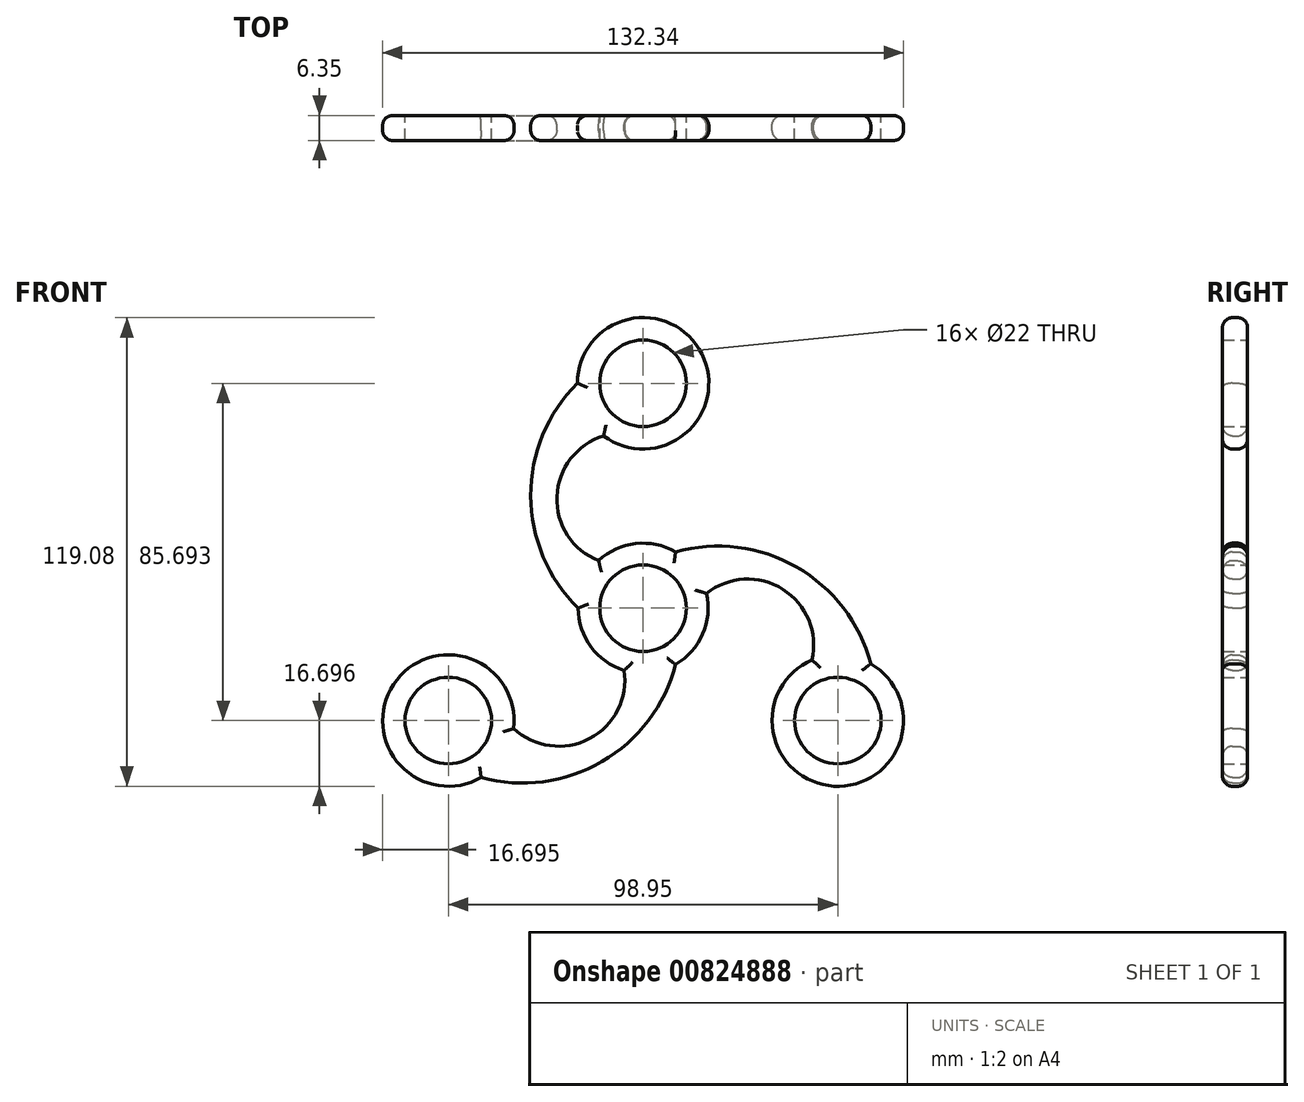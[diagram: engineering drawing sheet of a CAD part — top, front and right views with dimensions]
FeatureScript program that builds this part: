
annotation { "Feature Type Name" : "Feature", "Feature Type Description" : "" }
export const myFeature = defineFeature(function(context is Context, id is Id, definition is map)
    precondition{}
    {
        {
            var Q0;
            Q0=qCreatedBy(makeId("Front.planeOp"),FACE);
            var sketch = newSketch(context, id + "F0", { "sketchPlane" : qUnion([Q0])});
            skCircle(sketch, "E0", {"center": v(0, 0) * mm, "radius": 11 * mm});
            skCircle(sketch, "E1", {"center": v(0, 57.13) * mm, "radius": 11 * mm});
            skArc(sketch, "E2", {"start": v(-16.5, 0) * mm, "mid": v(-13.26, -9.82) * mm, "end": v(-4.8, -15.79) * mm});
            skArc(sketch, "E3", {"start": v(-10.01, 43.77) * mm, "mid": v(14.94, 64.59) * mm, "end": v(-16.7, 57.15) * mm});
            skArc(sketch, "E4", {"start": v(-16.7, 57.15) * mm, "mid": v(-28.55, 28.54) * mm, "end": v(-16.5, 0) * mm});
            skArc(sketch, "E5", {"start": v(-10.01, 43.77) * mm, "mid": v(-21.9, 28.36) * mm, "end": v(-11.27, 12.06) * mm});
            skArc(sketch, "E6.1.0", {"start": v(-32.9, -30.56) * mm, "mid": v(-63.4, -19.36) * mm, "end": v(-41.15, -43.03) * mm});
            skCircle(sketch, "E6.1.1", {"center": v(-49.47, -28.56) * mm, "radius": 11 * mm});
            skArc(sketch, "E6.1.2", {"start": v(-41.15, -43.03) * mm, "mid": v(-10.44, -38.99) * mm, "end": v(8.25, -14.3) * mm});
            skArc(sketch, "E6.1.3", {"start": v(-32.9, -30.56) * mm, "mid": v(-13.61, -33.15) * mm, "end": v(-4.8, -15.79) * mm});
            skArc(sketch, "E6.2.0", {"start": v(42.91, -13.21) * mm, "mid": v(48.47, -45.23) * mm, "end": v(57.84, -14.12) * mm});
            skCircle(sketch, "E6.2.1", {"center": v(49.47, -28.56) * mm, "radius": 11 * mm});
            skArc(sketch, "E6.2.2", {"start": v(57.84, -14.12) * mm, "mid": v(38.99, 10.45) * mm, "end": v(8.25, 14.3) * mm});
            skArc(sketch, "E6.2.3", {"start": v(42.91, -13.21) * mm, "mid": v(35.51, 4.78) * mm, "end": v(16.08, 3.73) * mm});
            skArc(sketch, "E7.trimOffspring", {"start": v(8.25, 14.3) * mm, "mid": v(-1.88, 16.4) * mm, "end": v(-11.27, 12.06) * mm});
            skArc(sketch, "E8.trimOffspring", {"start": v(8.25, -14.3) * mm, "mid": v(15.14, -6.57) * mm, "end": v(16.08, 3.73) * mm});
            skSolve(sketch);
        }
        {
            var Q0;
            Q0=makeQuery(id+"F0.imprint","IMPRINT",FACE,{"disambiguationData":[TD([[makeQuery(id+"F0.imprint","IMPRINT",EDGE,{"derivedFrom":sQuery(id+"F0.wireOp",EDGE,"E0")}),-1.0]])]});
            extrude(context, id + "F1", {"entities" : qUnion([Q0]), "depth" : 6.35 * mm, "offsetDistance" : 25.4 * mm});
        }
        {
            var Q0;
            Q0=makeQuery(id+"F1.opExtrude","CAP_EDGE",EDGE,{"disambiguationData":[OSD([sQuery(id+"F0.wireOp",EDGE,"E6.2.2")])],"isStart":false});
            var Q1;
            Q1=makeQuery(id+"F1.opExtrude","CAP_EDGE",EDGE,{"disambiguationData":[OSD([sQuery(id+"F0.wireOp",EDGE,"E6.2.0")])],"isStart":false});
            var Q2;
            Q2=makeQuery(id+"F1.opExtrude","CAP_EDGE",EDGE,{"disambiguationData":[OSD([sQuery(id+"F0.wireOp",EDGE,"E6.2.3")])],"isStart":false});
            var Q3;
            Q3=makeQuery(id+"F1.opExtrude","CAP_EDGE",EDGE,{"disambiguationData":[OSD([sQuery(id+"F0.wireOp",EDGE,"E7.trimOffspring")])],"isStart":false});
            var Q4;
            Q4=makeQuery(id+"F1.opExtrude","CAP_EDGE",EDGE,{"disambiguationData":[OSD([sQuery(id+"F0.wireOp",EDGE,"E8.trimOffspring")])],"isStart":false});
            var Q5;
            Q5=makeQuery(id+"F1.opExtrude","CAP_EDGE",EDGE,{"disambiguationData":[OSD([sQuery(id+"F0.wireOp",EDGE,"E6.1.2")])],"isStart":false});
            var Q6;
            Q6=makeQuery(id+"F1.opExtrude","CAP_EDGE",EDGE,{"disambiguationData":[OSD([sQuery(id+"F0.wireOp",EDGE,"E6.1.3")])],"isStart":false});
            var Q7;
            Q7=makeQuery(id+"F1.opExtrude","CAP_EDGE",EDGE,{"disambiguationData":[OSD([sQuery(id+"F0.wireOp",EDGE,"E2")])],"isStart":false});
            var Q8;
            Q8=makeQuery(id+"F1.opExtrude","CAP_EDGE",EDGE,{"disambiguationData":[OSD([sQuery(id+"F0.wireOp",EDGE,"E4")])],"isStart":false});
            var Q9;
            Q9=makeQuery(id+"F1.opExtrude","CAP_EDGE",EDGE,{"disambiguationData":[OSD([sQuery(id+"F0.wireOp",EDGE,"E5")])],"isStart":false});
            var Q10;
            Q10=makeQuery(id+"F1.opExtrude","CAP_EDGE",EDGE,{"disambiguationData":[OSD([sQuery(id+"F0.wireOp",EDGE,"E6.1.0")])],"isStart":false});
            var Q11;
            Q11=makeQuery(id+"F1.opExtrude","CAP_EDGE",EDGE,{"disambiguationData":[OSD([sQuery(id+"F0.wireOp",EDGE,"E3")])],"isStart":false});
            fillet(context, id + "F2", {"entities" : qUnion([Q0, Q1, Q2, Q3, Q4, Q5, Q6, Q7, Q8, Q9, Q10, Q11]), "radius" : 2.54 * mm, "tangentPropagation" : true, "allowEdgeOverflow" : false});
        }
        {
            var Q0;
            Q0=makeQuery(id+"F1.opExtrude","CAP_EDGE",EDGE,{"disambiguationData":[OSD([sQuery(id+"F0.wireOp",EDGE,"E3")])],"isStart":true});
            var Q1;
            Q1=makeQuery(id+"F1.opExtrude","CAP_EDGE",EDGE,{"disambiguationData":[OSD([sQuery(id+"F0.wireOp",EDGE,"E4")])],"isStart":true});
            var Q2;
            Q2=makeQuery(id+"F1.opExtrude","CAP_EDGE",EDGE,{"disambiguationData":[OSD([sQuery(id+"F0.wireOp",EDGE,"E5")])],"isStart":true});
            var Q3;
            Q3=makeQuery(id+"F1.opExtrude","CAP_EDGE",EDGE,{"disambiguationData":[OSD([sQuery(id+"F0.wireOp",EDGE,"E7.trimOffspring")])],"isStart":true});
            var Q4;
            Q4=makeQuery(id+"F1.opExtrude","CAP_EDGE",EDGE,{"disambiguationData":[OSD([sQuery(id+"F0.wireOp",EDGE,"E6.2.2")])],"isStart":true});
            var Q5;
            Q5=makeQuery(id+"F1.opExtrude","CAP_EDGE",EDGE,{"disambiguationData":[OSD([sQuery(id+"F0.wireOp",EDGE,"E6.2.3")])],"isStart":true});
            var Q6;
            Q6=makeQuery(id+"F1.opExtrude","CAP_EDGE",EDGE,{"disambiguationData":[OSD([sQuery(id+"F0.wireOp",EDGE,"E6.2.0")])],"isStart":true});
            var Q7;
            Q7=makeQuery(id+"F1.opExtrude","CAP_EDGE",EDGE,{"disambiguationData":[OSD([sQuery(id+"F0.wireOp",EDGE,"E6.1.2")])],"isStart":true});
            var Q8;
            Q8=makeQuery(id+"F1.opExtrude","CAP_EDGE",EDGE,{"disambiguationData":[OSD([sQuery(id+"F0.wireOp",EDGE,"E8.trimOffspring")])],"isStart":true});
            var Q9;
            Q9=makeQuery(id+"F1.opExtrude","CAP_EDGE",EDGE,{"disambiguationData":[OSD([sQuery(id+"F0.wireOp",EDGE,"E2")])],"isStart":true});
            var Q10;
            Q10=makeQuery(id+"F1.opExtrude","CAP_EDGE",EDGE,{"disambiguationData":[OSD([sQuery(id+"F0.wireOp",EDGE,"E6.1.3")])],"isStart":true});
            var Q11;
            Q11=makeQuery(id+"F1.opExtrude","CAP_EDGE",EDGE,{"disambiguationData":[OSD([sQuery(id+"F0.wireOp",EDGE,"E6.1.0")])],"isStart":true});
            fillet(context, id + "F3", {"entities" : qUnion([Q0, Q1, Q2, Q3, Q4, Q5, Q6, Q7, Q8, Q9, Q10, Q11]), "radius" : 2.54 * mm, "tangentPropagation" : true, "allowEdgeOverflow" : false});
        }
    });
